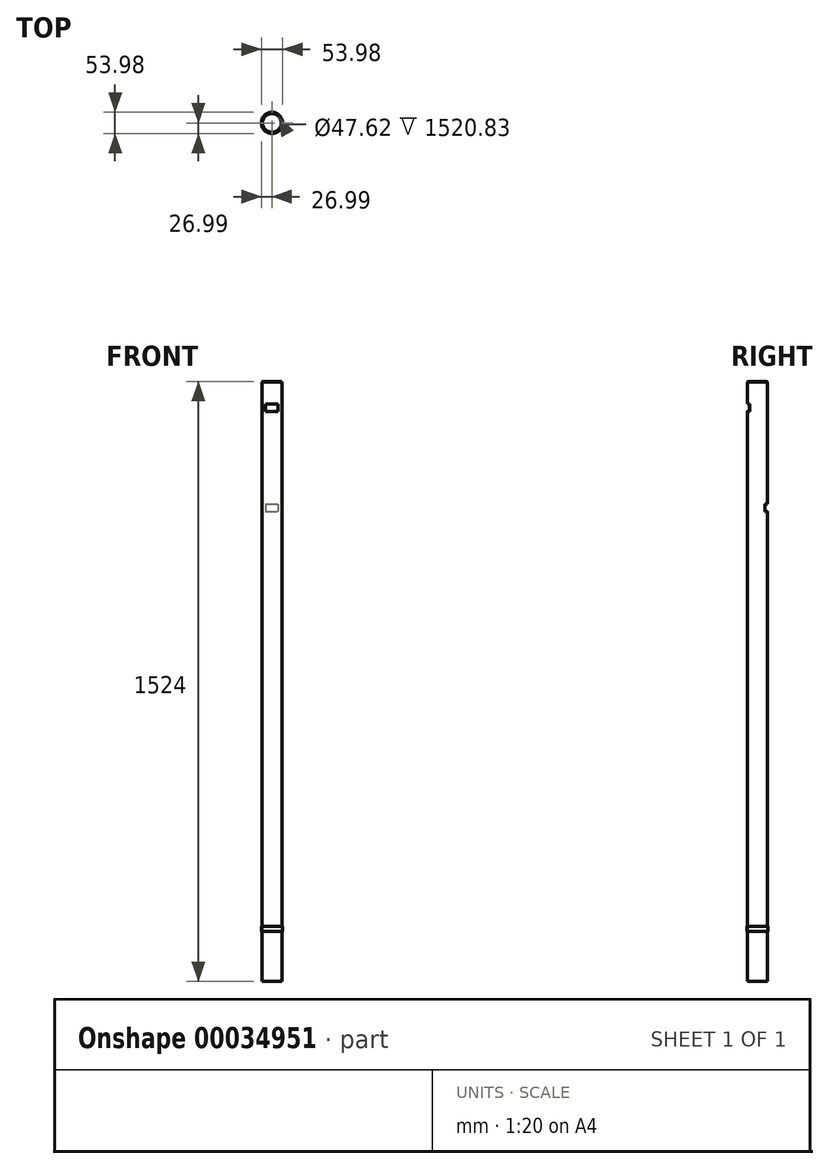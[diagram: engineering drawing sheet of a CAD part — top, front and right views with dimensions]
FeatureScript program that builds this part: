
annotation { "Feature Type Name" : "Feature", "Feature Type Description" : "" }
export const myFeature = defineFeature(function(context is Context, id is Id, definition is map)
    precondition{}
    {
        {
            var Q0;
            Q0=qCreatedBy(makeId("Top.planeOp"),FACE);
            var sketch = newSketch(context, id + "F0", { "sketchPlane" : qUnion([Q0])});
            skCircle(sketch, "E0", {"center": v(0, 0) * mm, "radius": 25.4 * mm});
            skCircle(sketch, "E1", {"center": v(0, 0) * mm, "radius": 23.81 * mm});
            skCircle(sketch, "E2", {"center": v(0, 0) * mm, "radius": 26.99 * mm});
            skSolve(sketch);
        }
        {
            var Q0;
            Q0=makeQuery(id+"F0.imprint","IMPRINT",FACE,{"disambiguationData":[TD([[makeQuery(id+"F0.imprint","IMPRINT",EDGE,{"derivedFrom":sQuery(id+"F0.wireOp",EDGE,"E1")}),1.0]])]});
            var Q1;
            Q1=makeQuery(id+"F0.imprint","IMPRINT",FACE,{"disambiguationData":[TD([[makeQuery(id+"F0.imprint","IMPRINT",EDGE,{"derivedFrom":sQuery(id+"F0.wireOp",EDGE,"E0")}),1.0]])]});
            extrude(context, id + "F1", {"entities" : qUnion([Q0, Q1]), "depth" : 1524 * mm});
        }
        {
            var Q0;
            Q0=makeQuery(id+"F0.imprint","IMPRINT",FACE,{"disambiguationData":[TD([[makeQuery(id+"F0.imprint","IMPRINT",EDGE,{"derivedFrom":sQuery(id+"F0.wireOp",EDGE,"E1")}),1.0]])]});
            extrude(context, id + "F2", {"entities" : qUnion([Q0]), "operationType" : NewBodyOperationType.REMOVE, "depth" : 1520.82 * mm});
        }
        {
            var Q0;
            Q0=makeQuery(id+"F1.opExtrude","CAP_EDGE",EDGE,{"disambiguationData":[OSD([sQuery(id+"F0.wireOp",EDGE,"E0")])],"isStart":false});
            chamfer(context, id + "F3", {"entities" : qUnion([Q0]), "width" : 1.59 * mm, "tangentPropagation" : true});
        }
        {
            var Q0;
            Q0=qCreatedBy(makeId("Front.planeOp"),FACE);
            var sketch = newSketch(context, id + "F4", { "sketchPlane" : qUnion([Q0])});
            skLineSegment(sketch, "E3.rect.bottom", {"start": v(-15.88, 1212.85) * mm, "end": v(15.88, 1212.85) * mm});
            skLineSegment(sketch, "E3.rect.top", {"start": v(-15.88, 1193.8) * mm, "end": v(15.87, 1193.8) * mm});
            skLineSegment(sketch, "E3.rect.left", {"start": v(-15.87, 1212.85) * mm, "end": v(-15.87, 1193.8) * mm});
            skLineSegment(sketch, "E3.rect.right", {"start": v(15.88, 1212.85) * mm, "end": v(15.88, 1193.8) * mm});
            skPoint(sketch, "E3.rect.middle", {"position": v(0, 1203.33) * mm});
            skLineSegment(sketch, "E4.rect.bottom", {"start": v(-15.87, 1466.85) * mm, "end": v(15.88, 1466.85) * mm});
            skLineSegment(sketch, "E4.rect.top", {"start": v(-15.87, 1447.8) * mm, "end": v(15.88, 1447.8) * mm});
            skLineSegment(sketch, "E4.rect.left", {"start": v(-15.87, 1466.85) * mm, "end": v(-15.87, 1447.8) * mm});
            skLineSegment(sketch, "E4.rect.right", {"start": v(15.88, 1466.85) * mm, "end": v(15.88, 1447.8) * mm});
            skPoint(sketch, "E4.rect.middle", {"position": v(0, 1457.33) * mm});
            skPoint(sketch, "E4.rect.middle.positionSnap0", {"position": v(0, 1212.85) * mm});
            skPoint(sketch, "E4.rect.centerSnap0", {"position": v(0, 1212.85) * mm});
            skSolve(sketch);
        }
        {
            var Q0;
            Q0=makeQuery(id+"F4.imprint","IMPRINT",FACE,{"disambiguationData":[TD([[makeQuery(id+"F4.imprint","IMPRINT",EDGE,{"derivedFrom":sQuery(id+"F4.wireOp",EDGE,"E3.rect.bottom")}),-1.0]])]});
            extrude(context, id + "F5", {"entities" : qUnion([Q0]), "operationType" : NewBodyOperationType.REMOVE, "oppositeDirection" : true, "depth" : 50.8 * mm});
        }
        {
            var Q0;
            Q0=makeQuery(id+"F0.imprint","IMPRINT",FACE,{"disambiguationData":[TD([[makeQuery(id+"F0.imprint","IMPRINT",EDGE,{"derivedFrom":sQuery(id+"F0.wireOp",EDGE,"E0")}),-1.0]])]});
            extrude(context, id + "F6", {"entities" : qUnion([Q0]), "operationType" : NewBodyOperationType.ADD, "depth" : 139.7 * mm, "hasSecondDirection" : true, "secondDirectionOppositeDirection" : false, "secondDirectionDepth" : 127 * mm});
        }
        {
            var Q0;
            Q0=makeQuery(id+"F4.imprint","IMPRINT",FACE,{"disambiguationData":[TD([[makeQuery(id+"F4.imprint","IMPRINT",EDGE,{"derivedFrom":sQuery(id+"F4.wireOp",EDGE,"E4.rect.bottom")}),-1.0]])]});
            extrude(context, id + "F7", {"entities" : qUnion([Q0]), "operationType" : NewBodyOperationType.REMOVE, "depth" : 139.7 * mm});
        }
    });
